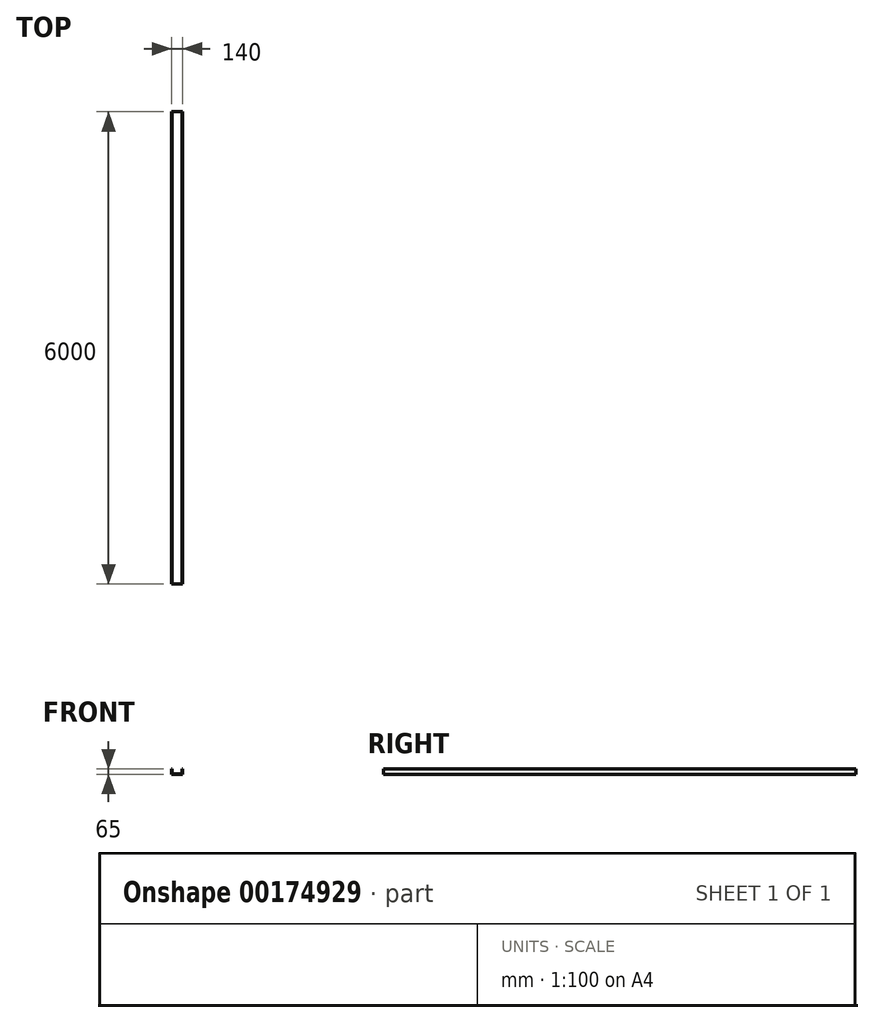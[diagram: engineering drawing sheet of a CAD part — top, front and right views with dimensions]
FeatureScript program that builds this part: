
annotation { "Feature Type Name" : "Feature", "Feature Type Description" : "" }
export const myFeature = defineFeature(function(context is Context, id is Id, definition is map)
    precondition{}
    {
        {
            var Q0;
            Q0=qCreatedBy(makeId("Front.planeOp"),FACE);
            var sketch = newSketch(context, id + "F0", { "sketchPlane" : qUnion([Q0])});
            skLineSegment(sketch, "E0", {"start": v(0, 0) * mm, "end": v(140, 0) * mm});
            skLineSegment(sketch, "E1", {"start": v(140, 0) * mm, "end": v(140, 65) * mm});
            skLineSegment(sketch, "E2", {"start": v(140, 65) * mm, "end": v(131, 65) * mm});
            skLineSegment(sketch, "E3", {"start": v(131, 65) * mm, "end": v(131, 5) * mm});
            skLineSegment(sketch, "E4", {"start": v(131, 5) * mm, "end": v(9, 5) * mm});
            skLineSegment(sketch, "E5", {"start": v(9, 5) * mm, "end": v(9, 65) * mm});
            skLineSegment(sketch, "E6", {"start": v(9, 65) * mm, "end": v(0, 65) * mm});
            skLineSegment(sketch, "E7", {"start": v(0, 65) * mm, "end": v(0, 0) * mm});
            skSolve(sketch);
        }
        {
            var Q0;
            Q0=qSketchRegion(id+"F0",true);
            extrude(context, id + "F1", {"entities" : qUnion([Q0]), "depth" : 6000 * mm});
        }
    });
